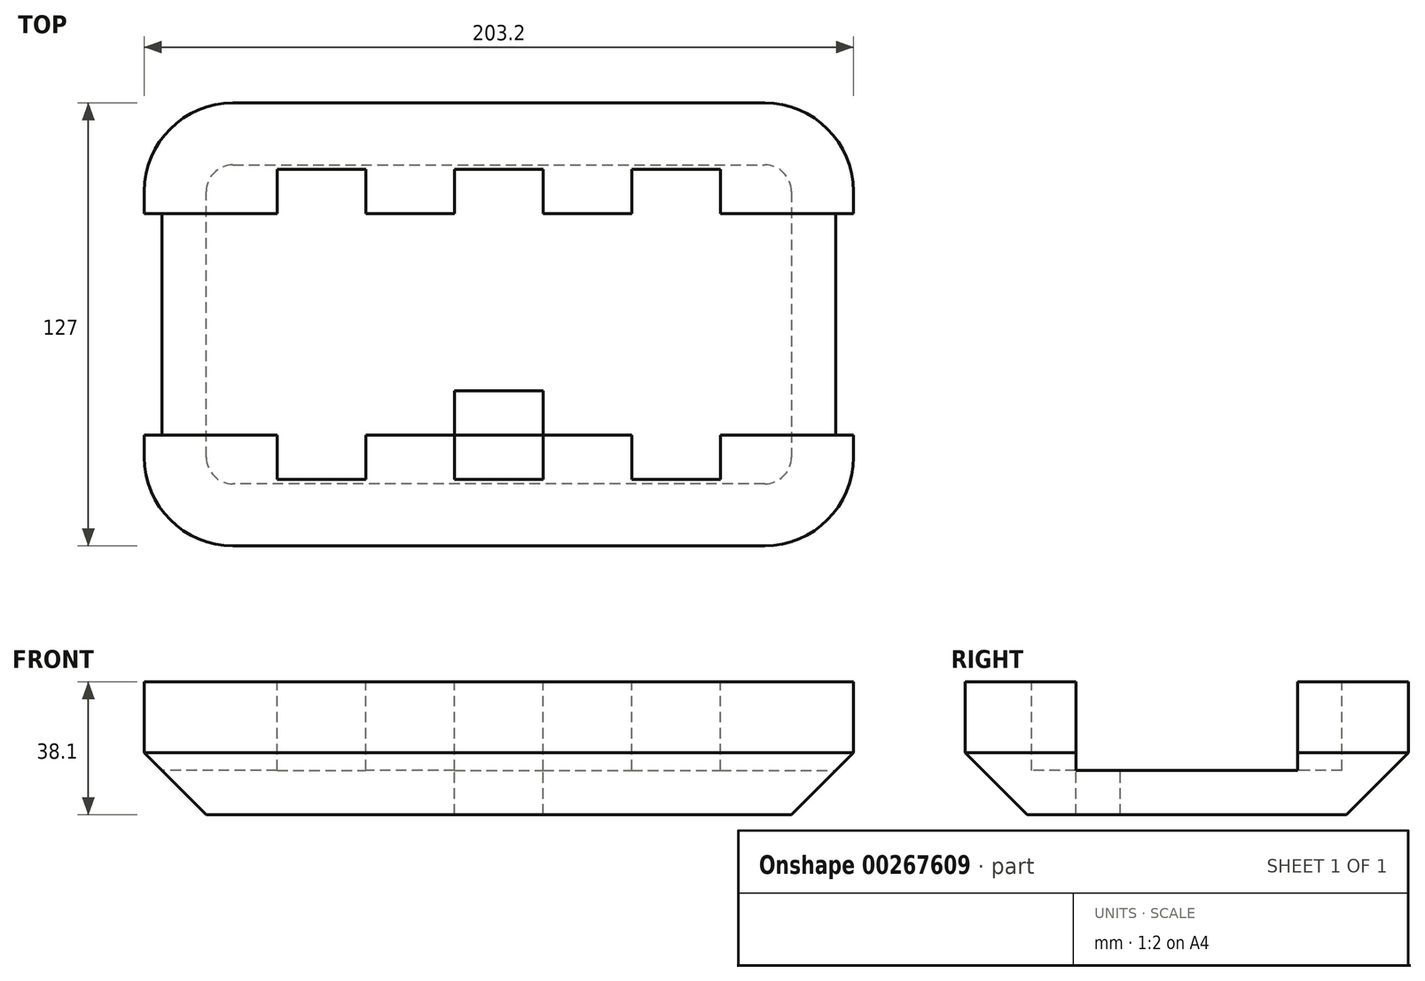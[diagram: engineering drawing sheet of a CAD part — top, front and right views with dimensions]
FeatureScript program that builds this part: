
annotation { "Feature Type Name" : "Feature", "Feature Type Description" : "" }
export const myFeature = defineFeature(function(context is Context, id is Id, definition is map)
    precondition{}
    {
        {
            var Q0;
            Q0=qCreatedBy(makeId("Top.planeOp"),FACE);
            var sketch = newSketch(context, id + "F0", { "sketchPlane" : qUnion([Q0])});
            skLineSegment(sketch, "E0.bottom", {"start": v(-101.6, 63.5) * mm, "end": v(101.6, 63.5) * mm});
            skLineSegment(sketch, "E0.top", {"start": v(-101.6, -63.5) * mm, "end": v(101.6, -63.5) * mm});
            skLineSegment(sketch, "E0.left", {"start": v(-101.6, 63.5) * mm, "end": v(-101.6, -63.5) * mm});
            skLineSegment(sketch, "E0.right", {"start": v(101.6, 63.5) * mm, "end": v(101.6, -63.5) * mm});
            skPoint(sketch, "E0.middle", {"position": v(0, 0) * mm});
            skLineSegment(sketch, "E1", {"start": v(0, 0) * mm, "end": v(0, 31.75) * mm});
            skLineSegment(sketch, "E2", {"start": v(0, 31.75) * mm, "end": v(-101.6, 31.75) * mm});
            skLineSegment(sketch, "E3", {"start": v(-101.6, 31.75) * mm, "end": v(101.6, 31.75) * mm});
            skLineSegment(sketch, "E4", {"start": v(0, 0) * mm, "end": v(0, -31.75) * mm});
            skLineSegment(sketch, "E5", {"start": v(0, -31.75) * mm, "end": v(-101.6, -31.75) * mm});
            skLineSegment(sketch, "E6", {"start": v(0, -31.75) * mm, "end": v(101.6, -31.75) * mm});
            skLineSegment(sketch, "E7", {"start": v(0, 31.75) * mm, "end": v(-50.8, 31.75) * mm});
            skLineSegment(sketch, "E8", {"start": v(0, 31.75) * mm, "end": v(50.8, 31.75) * mm});
            skLineSegment(sketch, "E9", {"start": v(0, -31.75) * mm, "end": v(50.8, -31.75) * mm});
            skLineSegment(sketch, "E10", {"start": v(50.8, -31.75) * mm, "end": v(-50.8, -31.75) * mm});
            skLineSegment(sketch, "E11.bottom", {"start": v(-63.5, 44.45) * mm, "end": v(-38.1, 44.45) * mm});
            skLineSegment(sketch, "E11.top", {"start": v(-63.5, 19.05) * mm, "end": v(-38.1, 19.05) * mm});
            skLineSegment(sketch, "E11.left", {"start": v(-63.5, 44.45) * mm, "end": v(-63.5, 19.05) * mm});
            skLineSegment(sketch, "E11.right", {"start": v(-38.1, 44.45) * mm, "end": v(-38.1, 19.05) * mm});
            skPoint(sketch, "E11.middle", {"position": v(-50.8, 31.75) * mm});
            skLineSegment(sketch, "E12.bottom", {"start": v(-12.7, 44.45) * mm, "end": v(12.7, 44.45) * mm});
            skLineSegment(sketch, "E12.top", {"start": v(-12.7, 19.05) * mm, "end": v(12.7, 19.05) * mm});
            skLineSegment(sketch, "E12.left", {"start": v(-12.7, 44.45) * mm, "end": v(-12.7, 19.05) * mm});
            skLineSegment(sketch, "E12.right", {"start": v(12.7, 44.45) * mm, "end": v(12.7, 19.05) * mm});
            skPoint(sketch, "E12.middle", {"position": v(0, 31.75) * mm});
            skLineSegment(sketch, "E13.bottom", {"start": v(38.1, 44.45) * mm, "end": v(63.5, 44.45) * mm});
            skLineSegment(sketch, "E13.top", {"start": v(38.1, 19.05) * mm, "end": v(63.5, 19.05) * mm});
            skLineSegment(sketch, "E13.left", {"start": v(38.1, 44.45) * mm, "end": v(38.1, 19.05) * mm});
            skLineSegment(sketch, "E13.right", {"start": v(63.5, 44.45) * mm, "end": v(63.5, 19.05) * mm});
            skPoint(sketch, "E13.middle", {"position": v(50.8, 31.75) * mm});
            skLineSegment(sketch, "E14.bottom", {"start": v(-12.7, -19.05) * mm, "end": v(12.7, -19.05) * mm});
            skLineSegment(sketch, "E14.top", {"start": v(-12.7, -44.45) * mm, "end": v(12.7, -44.45) * mm});
            skLineSegment(sketch, "E14.left", {"start": v(-12.7, -19.05) * mm, "end": v(-12.7, -44.45) * mm});
            skLineSegment(sketch, "E14.right", {"start": v(12.7, -19.05) * mm, "end": v(12.7, -44.45) * mm});
            skPoint(sketch, "E14.middle", {"position": v(0, -31.75) * mm});
            skLineSegment(sketch, "E15.bottom", {"start": v(-63.5, -19.05) * mm, "end": v(-38.1, -19.05) * mm});
            skLineSegment(sketch, "E15.top", {"start": v(-63.5, -44.45) * mm, "end": v(-38.1, -44.45) * mm});
            skLineSegment(sketch, "E15.left", {"start": v(-63.5, -19.05) * mm, "end": v(-63.5, -44.45) * mm});
            skLineSegment(sketch, "E15.right", {"start": v(-38.1, -19.05) * mm, "end": v(-38.1, -44.45) * mm});
            skPoint(sketch, "E15.middle", {"position": v(-50.8, -31.75) * mm});
            skLineSegment(sketch, "E16.bottom", {"start": v(38.1, -19.05) * mm, "end": v(63.5, -19.05) * mm});
            skLineSegment(sketch, "E16.top", {"start": v(38.1, -44.45) * mm, "end": v(63.5, -44.45) * mm});
            skLineSegment(sketch, "E16.left", {"start": v(38.1, -19.05) * mm, "end": v(38.1, -44.45) * mm});
            skLineSegment(sketch, "E16.right", {"start": v(63.5, -19.05) * mm, "end": v(63.5, -44.45) * mm});
            skPoint(sketch, "E16.middle", {"position": v(50.8, -31.75) * mm});
            skSolve(sketch);
        }
        {
            var Q0;
            {var subQ18=sQuery(id+"F0.wireOp",EDGE,"E0.bottom");Q0=makeQuery(id+"F0.imprint","IMPRINT",FACE,{"disambiguationData":[TD([[makeQuery(id+"F0.imprint","IMPRINT",EDGE,{"derivedFrom":subQ18}),-1.0]])]});}
            var Q1;
            {var subQ1=sQuery(id+"F0.wireOp",EDGE,"E11.top");Q1=makeQuery(id+"F0.imprint","IMPRINT",FACE,{"disambiguationData":[TD([[makeQuery(id+"F0.imprint","IMPRINT",EDGE,{"derivedFrom":subQ1}),-1.0]])]});}
            var Q2;
            {var subQ16=sQuery(id+"F0.wireOp",EDGE,"E13.top");Q2=makeQuery(id+"F0.imprint","IMPRINT",FACE,{"disambiguationData":[TD([[makeQuery(id+"F0.imprint","IMPRINT",EDGE,{"derivedFrom":subQ16}),-1.0]])]});}
            var Q3;
            {var subQ15=sQuery(id+"F0.wireOp",EDGE,"E0.top");Q3=makeQuery(id+"F0.imprint","IMPRINT",FACE,{"disambiguationData":[TD([[makeQuery(id+"F0.imprint","IMPRINT",EDGE,{"derivedFrom":subQ15}),1.0]])]});}
            var Q4;
            {var subQ0=sQuery(id+"F0.wireOp",EDGE,"E11.top");Q4=makeQuery(id+"F0.imprint","IMPRINT",FACE,{"disambiguationData":[TD([[makeQuery(id+"F0.imprint","IMPRINT",EDGE,{"derivedFrom":subQ0}),1.0]])]});}
            var Q5;
            {var subQ0=sQuery(id+"F0.wireOp",EDGE,"E11.bottom");Q5=makeQuery(id+"F0.imprint","IMPRINT",FACE,{"disambiguationData":[TD([[makeQuery(id+"F0.imprint","IMPRINT",EDGE,{"derivedFrom":subQ0}),-1.0]])]});}
            var Q6;
            {var subQ1=sQuery(id+"F0.wireOp",EDGE,"E12.bottom");Q6=makeQuery(id+"F0.imprint","IMPRINT",FACE,{"disambiguationData":[TD([[makeQuery(id+"F0.imprint","IMPRINT",EDGE,{"derivedFrom":subQ1}),-1.0]])]});}
            var Q7;
            {var subQ3=sQuery(id+"F0.wireOp",EDGE,"E12.top");var subQ5=sQuery(id+"F0.wireOp",EDGE,"E12.left");var subQ7=makeQuery(id+"F0.imprint","INTERSECT",VERTEX,{"derivedFrom":[subQ3,subQ5]});Q7=makeQuery(id+"F0.imprint","IMPRINT",FACE,{"disambiguationData":[TD([[makeQuery(id+"F0.imprint","IMPRINT",EDGE,{"disambiguationData":[TD([[subQ7,-1.0]])],"derivedFrom":subQ3}),1.0]])]});}
            var Q8;
            {var subQ3=sQuery(id+"F0.wireOp",EDGE,"E12.top");var subQ5=sQuery(id+"F0.wireOp",EDGE,"E12.right");var subQ6=makeQuery(id+"F0.imprint","INTERSECT",VERTEX,{"derivedFrom":[subQ3,subQ5]});Q8=makeQuery(id+"F0.imprint","IMPRINT",FACE,{"disambiguationData":[TD([[makeQuery(id+"F0.imprint","IMPRINT",EDGE,{"disambiguationData":[TD([[subQ6,1.0]])],"derivedFrom":subQ3}),1.0]])]});}
            var Q9;
            {var subQ1=sQuery(id+"F0.wireOp",EDGE,"E13.top");Q9=makeQuery(id+"F0.imprint","IMPRINT",FACE,{"disambiguationData":[TD([[makeQuery(id+"F0.imprint","IMPRINT",EDGE,{"derivedFrom":subQ1}),1.0]])]});}
            var Q10;
            {var subQ1=sQuery(id+"F0.wireOp",EDGE,"E13.bottom");Q10=makeQuery(id+"F0.imprint","IMPRINT",FACE,{"disambiguationData":[TD([[makeQuery(id+"F0.imprint","IMPRINT",EDGE,{"derivedFrom":subQ1}),-1.0]])]});}
            var Q11;
            {var subQ1=sQuery(id+"F0.wireOp",EDGE,"E16.bottom");Q11=makeQuery(id+"F0.imprint","IMPRINT",FACE,{"disambiguationData":[TD([[makeQuery(id+"F0.imprint","IMPRINT",EDGE,{"derivedFrom":subQ1}),-1.0]])]});}
            var Q12;
            {var subQ1=sQuery(id+"F0.wireOp",EDGE,"E16.top");Q12=makeQuery(id+"F0.imprint","IMPRINT",FACE,{"disambiguationData":[TD([[makeQuery(id+"F0.imprint","IMPRINT",EDGE,{"derivedFrom":subQ1}),1.0]])]});}
            var Q13;
            {var subQ1=sQuery(id+"F0.wireOp",EDGE,"E14.top");Q13=makeQuery(id+"F0.imprint","IMPRINT",FACE,{"disambiguationData":[TD([[makeQuery(id+"F0.imprint","IMPRINT",EDGE,{"derivedFrom":subQ1}),1.0]])]});}
            var Q14;
            {var subQ0=sQuery(id+"F0.wireOp",EDGE,"E10");var subQ1=sQuery(id+"F0.wireOp",EDGE,"E4");var subQ2=makeQuery(id+"F0.imprint","INTERSECT",VERTEX,{"derivedFrom":[subQ1,subQ0]});Q14=makeQuery(id+"F0.imprint","IMPRINT",FACE,{"disambiguationData":[TD([[makeQuery(id+"F0.imprint","IMPRINT",EDGE,{"disambiguationData":[TD([[subQ2,1.0]])],"derivedFrom":subQ1}),-1.0]])]});}
            var Q15;
            {var subQ0=sQuery(id+"F0.wireOp",EDGE,"E10");var subQ1=sQuery(id+"F0.wireOp",EDGE,"E4");var subQ2=makeQuery(id+"F0.imprint","INTERSECT",VERTEX,{"derivedFrom":[subQ1,subQ0]});Q15=makeQuery(id+"F0.imprint","IMPRINT",FACE,{"disambiguationData":[TD([[makeQuery(id+"F0.imprint","IMPRINT",EDGE,{"disambiguationData":[TD([[subQ2,1.0]])],"derivedFrom":subQ1}),1.0]])]});}
            var Q16;
            {var subQ1=sQuery(id+"F0.wireOp",EDGE,"E15.bottom");Q16=makeQuery(id+"F0.imprint","IMPRINT",FACE,{"disambiguationData":[TD([[makeQuery(id+"F0.imprint","IMPRINT",EDGE,{"derivedFrom":subQ1}),-1.0]])]});}
            var Q17;
            {var subQ0=sQuery(id+"F0.wireOp",EDGE,"E15.top");Q17=makeQuery(id+"F0.imprint","IMPRINT",FACE,{"disambiguationData":[TD([[makeQuery(id+"F0.imprint","IMPRINT",EDGE,{"derivedFrom":subQ0}),1.0]])]});}
            extrude(context, id + "F1", {"entities" : qUnion([Q0, Q1, Q2, Q3, Q4, Q5, Q6, Q7, Q8, Q9, Q10, Q11, Q12, Q13, Q14, Q15, Q16, Q17]), "oppositeDirection" : true, "depth" : 38.1 * mm});
        }
        {
            var Q0;
            {var subQ0=sQuery(id+"F0.wireOp",EDGE,"E11.bottom");Q0=makeQuery(id+"F0.imprint","IMPRINT",FACE,{"disambiguationData":[TD([[makeQuery(id+"F0.imprint","IMPRINT",EDGE,{"derivedFrom":subQ0}),-1.0]])]});}
            var Q1;
            {var subQ0=sQuery(id+"F0.wireOp",EDGE,"E11.top");Q1=makeQuery(id+"F0.imprint","IMPRINT",FACE,{"disambiguationData":[TD([[makeQuery(id+"F0.imprint","IMPRINT",EDGE,{"derivedFrom":subQ0}),1.0]])]});}
            var Q2;
            {var subQ1=sQuery(id+"F0.wireOp",EDGE,"E15.bottom");Q2=makeQuery(id+"F0.imprint","IMPRINT",FACE,{"disambiguationData":[TD([[makeQuery(id+"F0.imprint","IMPRINT",EDGE,{"derivedFrom":subQ1}),-1.0]])]});}
            var Q3;
            {var subQ0=sQuery(id+"F0.wireOp",EDGE,"E15.top");Q3=makeQuery(id+"F0.imprint","IMPRINT",FACE,{"disambiguationData":[TD([[makeQuery(id+"F0.imprint","IMPRINT",EDGE,{"derivedFrom":subQ0}),1.0]])]});}
            var Q4;
            {var subQ0=sQuery(id+"F0.wireOp",EDGE,"E10");var subQ1=sQuery(id+"F0.wireOp",EDGE,"E4");var subQ2=makeQuery(id+"F0.imprint","INTERSECT",VERTEX,{"derivedFrom":[subQ1,subQ0]});Q4=makeQuery(id+"F0.imprint","IMPRINT",FACE,{"disambiguationData":[TD([[makeQuery(id+"F0.imprint","IMPRINT",EDGE,{"disambiguationData":[TD([[subQ2,1.0]])],"derivedFrom":subQ1}),-1.0]])]});}
            var Q5;
            {var subQ0=sQuery(id+"F0.wireOp",EDGE,"E10");var subQ1=sQuery(id+"F0.wireOp",EDGE,"E4");var subQ2=makeQuery(id+"F0.imprint","INTERSECT",VERTEX,{"derivedFrom":[subQ1,subQ0]});Q5=makeQuery(id+"F0.imprint","IMPRINT",FACE,{"disambiguationData":[TD([[makeQuery(id+"F0.imprint","IMPRINT",EDGE,{"disambiguationData":[TD([[subQ2,1.0]])],"derivedFrom":subQ1}),1.0]])]});}
            var Q6;
            {var subQ3=sQuery(id+"F0.wireOp",EDGE,"E12.top");var subQ5=sQuery(id+"F0.wireOp",EDGE,"E12.left");var subQ7=makeQuery(id+"F0.imprint","INTERSECT",VERTEX,{"derivedFrom":[subQ3,subQ5]});Q6=makeQuery(id+"F0.imprint","IMPRINT",FACE,{"disambiguationData":[TD([[makeQuery(id+"F0.imprint","IMPRINT",EDGE,{"disambiguationData":[TD([[subQ7,-1.0]])],"derivedFrom":subQ3}),1.0]])]});}
            var Q7;
            {var subQ3=sQuery(id+"F0.wireOp",EDGE,"E12.top");var subQ5=sQuery(id+"F0.wireOp",EDGE,"E12.right");var subQ6=makeQuery(id+"F0.imprint","INTERSECT",VERTEX,{"derivedFrom":[subQ3,subQ5]});Q7=makeQuery(id+"F0.imprint","IMPRINT",FACE,{"disambiguationData":[TD([[makeQuery(id+"F0.imprint","IMPRINT",EDGE,{"disambiguationData":[TD([[subQ6,1.0]])],"derivedFrom":subQ3}),1.0]])]});}
            var Q8;
            {var subQ1=sQuery(id+"F0.wireOp",EDGE,"E12.bottom");Q8=makeQuery(id+"F0.imprint","IMPRINT",FACE,{"disambiguationData":[TD([[makeQuery(id+"F0.imprint","IMPRINT",EDGE,{"derivedFrom":subQ1}),-1.0]])]});}
            var Q9;
            {var subQ1=sQuery(id+"F0.wireOp",EDGE,"E14.top");Q9=makeQuery(id+"F0.imprint","IMPRINT",FACE,{"disambiguationData":[TD([[makeQuery(id+"F0.imprint","IMPRINT",EDGE,{"derivedFrom":subQ1}),1.0]])]});}
            var Q10;
            {var subQ1=sQuery(id+"F0.wireOp",EDGE,"E16.top");Q10=makeQuery(id+"F0.imprint","IMPRINT",FACE,{"disambiguationData":[TD([[makeQuery(id+"F0.imprint","IMPRINT",EDGE,{"derivedFrom":subQ1}),1.0]])]});}
            var Q11;
            {var subQ1=sQuery(id+"F0.wireOp",EDGE,"E16.bottom");Q11=makeQuery(id+"F0.imprint","IMPRINT",FACE,{"disambiguationData":[TD([[makeQuery(id+"F0.imprint","IMPRINT",EDGE,{"derivedFrom":subQ1}),-1.0]])]});}
            var Q12;
            {var subQ1=sQuery(id+"F0.wireOp",EDGE,"E13.top");Q12=makeQuery(id+"F0.imprint","IMPRINT",FACE,{"disambiguationData":[TD([[makeQuery(id+"F0.imprint","IMPRINT",EDGE,{"derivedFrom":subQ1}),1.0]])]});}
            var Q13;
            {var subQ1=sQuery(id+"F0.wireOp",EDGE,"E13.bottom");Q13=makeQuery(id+"F0.imprint","IMPRINT",FACE,{"disambiguationData":[TD([[makeQuery(id+"F0.imprint","IMPRINT",EDGE,{"derivedFrom":subQ1}),-1.0]])]});}
            extrude(context, id + "F2", {"entities" : qUnion([Q0, Q1, Q2, Q3, Q4, Q5, Q6, Q7, Q8, Q9, Q10, Q11, Q12, Q13]), "operationType" : NewBodyOperationType.REMOVE, "oppositeDirection" : true, "depth" : 25.4 * mm});
        }
        {
            var Q0;
            Q0=makeQuery(id+"F1.opExtrude","SWEPT_EDGE",EDGE,{"disambiguationData":[OSD([sQuery(id+"F0.wireOp",EDGE,"E0.top"),sQuery(id+"F0.wireOp",EDGE,"E0.left")])]});
            var Q1;
            Q1=makeQuery(id+"F1.opExtrude","SWEPT_EDGE",EDGE,{"disambiguationData":[OSD([sQuery(id+"F0.wireOp",EDGE,"E0.top"),sQuery(id+"F0.wireOp",EDGE,"E0.right")])]});
            var Q2;
            Q2=makeQuery(id+"F1.opExtrude","SWEPT_EDGE",EDGE,{"disambiguationData":[OSD([sQuery(id+"F0.wireOp",EDGE,"E0.bottom"),sQuery(id+"F0.wireOp",EDGE,"E0.right")])]});
            var Q3;
            Q3=makeQuery(id+"F1.opExtrude","SWEPT_EDGE",EDGE,{"disambiguationData":[OSD([sQuery(id+"F0.wireOp",EDGE,"E0.bottom"),sQuery(id+"F0.wireOp",EDGE,"E0.left")])]});
            fillet(context, id + "F3", {"entities" : qUnion([Q0, Q1, Q2, Q3]), "radius" : 25.4 * mm, "tangentPropagation" : true, "allowEdgeOverflow" : false});
        }
        {
            var Q0;
            Q0=makeQuery(id+"F1.opExtrude","CAP_EDGE",EDGE,{"disambiguationData":[OSD([sQuery(id+"F0.wireOp",EDGE,"E0.top")])],"isStart":false});
            chamfer(context, id + "F4", {"entities" : qUnion([Q0]), "width" : 17.78 * mm, "tangentPropagation" : true});
        }
    });
